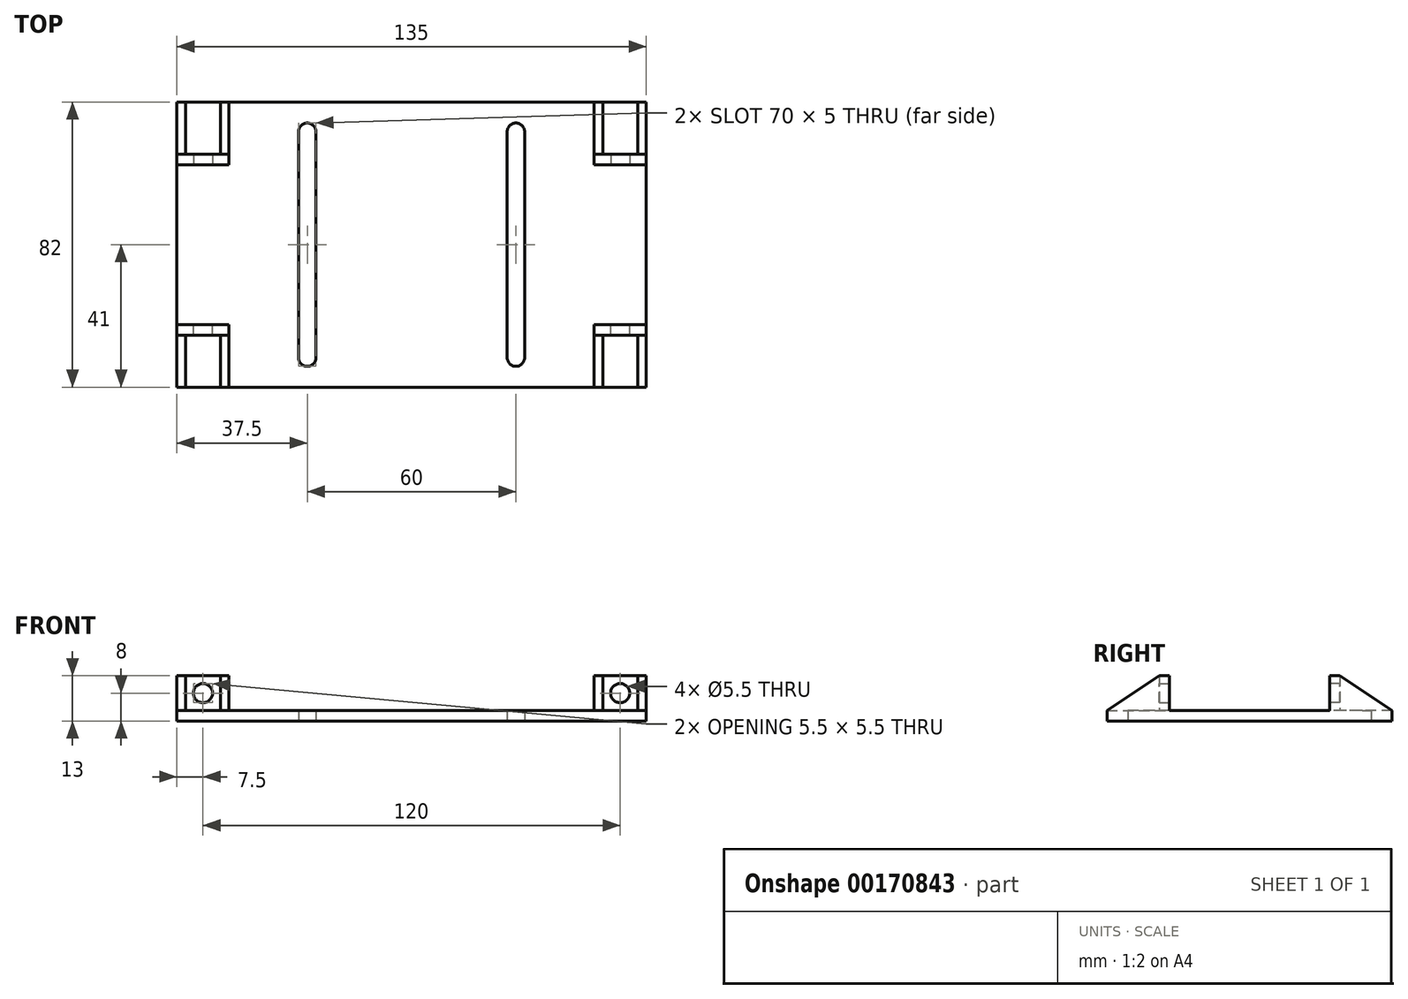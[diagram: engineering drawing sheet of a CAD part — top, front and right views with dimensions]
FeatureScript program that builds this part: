
annotation { "Feature Type Name" : "Feature", "Feature Type Description" : "" }
export const myFeature = defineFeature(function(context is Context, id is Id, definition is map)
    precondition{}
    {
        {
            var Q0;
            Q0=qCreatedBy(makeId("Top.planeOp"),FACE);
            var sketch = newSketch(context, id + "F0", { "sketchPlane" : qUnion([Q0])});
            skLineSegment(sketch, "E0", {"start": v(-67.5, -41) * mm, "end": v(67.5, -41) * mm});
            skLineSegment(sketch, "E1", {"start": v(67.5, -41) * mm, "end": v(67.5, 41) * mm});
            skLineSegment(sketch, "E2", {"start": v(67.5, 41) * mm, "end": v(-67.5, 41) * mm});
            skLineSegment(sketch, "E3", {"start": v(-67.5, 41) * mm, "end": v(-67.5, -41) * mm});
            skPoint(sketch, "E4", {"position": v(0, -41) * mm});
            skLineSegment(sketch, "E5.bottom", {"start": v(-30, 35) * mm, "end": v(-30, 35) * mm});
            skLineSegment(sketch, "E5.top", {"start": v(-30, -35) * mm, "end": v(-30, -35) * mm});
            skLineSegment(sketch, "E5.left", {"start": v(-32.5, 32.5) * mm, "end": v(-32.5, -32.5) * mm});
            skLineSegment(sketch, "E5.right", {"start": v(-27.5, 32.5) * mm, "end": v(-27.5, -32.5) * mm});
            skPoint(sketch, "E6", {"position": v(-67.5, 0) * mm});
            skLineSegment(sketch, "E7", {"start": v(-30, 71.7) * mm, "end": v(-30, -11.63) * mm, "construction": true});
            skPoint(sketch, "E7.startSnap0", {"position": v(-30, 35) * mm});
            skLineSegment(sketch, "E8", {"start": v(-39.4, 0) * mm, "end": v(-20.14, 0) * mm, "construction": true});
            skPoint(sketch, "E8.startSnap0", {"position": v(-32.5, 0) * mm});
            skPoint(sketch, "E9.visualSharp", {"position": v(-32.5, 35) * mm});
            skArc(sketch, "E9.filletArc", {"start": v(-30, 35) * mm, "mid": v(-31.77, 34.27) * mm, "end": v(-32.5, 32.5) * mm});
            skPoint(sketch, "E10.visualSharp", {"position": v(-27.5, 35) * mm});
            skArc(sketch, "E10.filletArc", {"start": v(-27.5, 32.5) * mm, "mid": v(-28.23, 34.27) * mm, "end": v(-30, 35) * mm});
            skPoint(sketch, "E11.visualSharp", {"position": v(-32.5, -35) * mm});
            skArc(sketch, "E11.filletArc", {"start": v(-32.5, -32.5) * mm, "mid": v(-31.77, -34.27) * mm, "end": v(-30, -35) * mm});
            skPoint(sketch, "E12.visualSharp", {"position": v(-27.5, -35) * mm});
            skArc(sketch, "E12.filletArc", {"start": v(-30, -35) * mm, "mid": v(-28.23, -34.27) * mm, "end": v(-27.5, -32.5) * mm});
            skLineSegment(sketch, "E13", {"start": v(0, -41) * mm, "end": v(0, 52.88) * mm, "construction": true});
            skPoint(sketch, "E13.endSnap0", {"position": v(0, 41) * mm});
            skArc(sketch, "E14.MirrorCS", {"start": v(27.5, 32.5) * mm, "mid": v(28.23, 34.27) * mm, "end": v(30, 35) * mm});
            skArc(sketch, "E15.MirrorCS", {"start": v(30, 35) * mm, "mid": v(31.77, 34.27) * mm, "end": v(32.5, 32.5) * mm});
            skLineSegment(sketch, "E16.MirrorCS", {"start": v(32.5, 32.5) * mm, "end": v(32.5, -32.5) * mm});
            skArc(sketch, "E17.MirrorCS", {"start": v(32.5, -32.5) * mm, "mid": v(31.77, -34.27) * mm, "end": v(30, -35) * mm});
            skLineSegment(sketch, "E18.MirrorCS", {"start": v(27.5, 32.5) * mm, "end": v(27.5, -32.5) * mm});
            skArc(sketch, "E19.MirrorCS", {"start": v(30, -35) * mm, "mid": v(28.23, -34.27) * mm, "end": v(27.5, -32.5) * mm});
            skSolve(sketch);
        }
        {
            var Q0;
            Q0=qSketchRegion(id+"F0",true);
            var Q1;
            Q1=makeQuery(id+"F0.imprint","IMPRINT",FACE,{"disambiguationData":[TD([[makeQuery(id+"F0.imprint","IMPRINT",EDGE,{"derivedFrom":sQuery(id+"F0.wireOp",EDGE,"T7wDZl8h-PH1E-OXKs-Syz4-WPVjGr0DlJHF")}),1.0]])]});
            extrude(context, id + "F1", {"entities" : qUnion([Q0, Q1]), "depth" : 3 * mm});
        }
        {
            var Q0;
            Q0=makeQuery(id+"F1.opExtrude","SWEPT_FACE",FACE,{"disambiguationData":[OSD([sQuery(id+"F0.wireOp",EDGE,"E1")])]});
            var sketch = newSketch(context, id + "F2", { "sketchPlane" : qUnion([Q0])});
            skLineSegment(sketch, "E20.bottom", {"start": v(-23, 3) * mm, "end": v(-26, 3) * mm});
            skLineSegment(sketch, "E20.top", {"start": v(-23, 13) * mm, "end": v(-26, 13) * mm});
            skLineSegment(sketch, "E20.left", {"start": v(-23, 3) * mm, "end": v(-23, 13) * mm});
            skLineSegment(sketch, "E20.right", {"start": v(-26, 3) * mm, "end": v(-26, 13) * mm});
            skLineSegment(sketch, "E21", {"start": v(-26, 13) * mm, "end": v(-41, 3) * mm});
            skLineSegment(sketch, "E22", {"start": v(-41, 3) * mm, "end": v(-26, 3) * mm});
            skSolve(sketch);
        }
        {
            var Q0;
            Q0=makeQuery(id+"F2.imprint","IMPRINT",FACE,{"disambiguationData":[TD([[makeQuery(id+"F2.imprint","IMPRINT",EDGE,{"derivedFrom":sQuery(id+"F2.wireOp",EDGE,"E20.bottom")}),1.0]])]});
            extrude(context, id + "F3", {"entities" : qUnion([Q0]), "operationType" : NewBodyOperationType.ADD, "oppositeDirection" : true, "depth" : 15 * mm});
        }
        {
            var Q0;
            Q0=makeQuery(id+"F2.imprint","IMPRINT",FACE,{"disambiguationData":[TD([[makeQuery(id+"F2.imprint","IMPRINT",EDGE,{"derivedFrom":sQuery(id+"F2.wireOp",EDGE,"E20.right")}),1.0]])]});
            extrude(context, id + "F4", {"entities" : qUnion([Q0]), "operationType" : NewBodyOperationType.ADD, "oppositeDirection" : true, "depth" : 15 * mm});
        }
        {
            var Q0;
            Q0=makeQuery(id+"F1.opExtrude","CAP_FACE",FACE,{"disambiguationData":[OSD([sQuery(id+"F0.wireOp",EDGE,"E0"),sQuery(id+"F0.wireOp",EDGE,"E1"),sQuery(id+"F0.wireOp",EDGE,"E2"),sQuery(id+"F0.wireOp",EDGE,"E3")])],"isStart":false});
            var sketch = newSketch(context, id + "F5", { "sketchPlane" : qUnion([Q0])});
            skLineSegment(sketch, "E23.bottom", {"start": v(65, -41) * mm, "end": v(55, -41) * mm});
            skLineSegment(sketch, "E23.top", {"start": v(65, -26) * mm, "end": v(55, -26) * mm});
            skLineSegment(sketch, "E23.left", {"start": v(65, -41) * mm, "end": v(65, -26) * mm});
            skLineSegment(sketch, "E23.right", {"start": v(55, -41) * mm, "end": v(55, -26) * mm});
            skSolve(sketch);
        }
        {
            var Q0;
            Q0=qSketchRegion(id+"F5",true);
            extrude(context, id + "F6", {"entities" : qUnion([Q0]), "operationType" : NewBodyOperationType.REMOVE, "depth" : 25 * mm});
        }
        {
            var Q0;
            Q0=makeQuery(id+"F3.opExtrude","SWEPT_FACE",FACE,{"disambiguationData":[OSD([sQuery(id+"F2.wireOp",EDGE,"E20.left")])]});
            var sketch = newSketch(context, id + "F7", { "sketchPlane" : qUnion([Q0])});
            skLineSegment(sketch, "E24", {"start": v(-52.5, 3) * mm, "end": v(-67.5, 13) * mm, "construction": true});
            skLineSegment(sketch, "E25", {"start": v(-52.5, 13) * mm, "end": v(-67.5, 3) * mm, "construction": true});
            skPoint(sketch, "E26", {"position": v(-60, 8) * mm});
            skSolve(sketch);
        }
        {
            var Q0;
            Q0=sQuery(id+"F7.wireOp",VERTEX,"E26");
            var Q1;
            Q1=makeQuery(id+"F3.opExtrude","SWEPT_BODY",BODY,{"disambiguationData":[OSD([sQuery(id+"F2.wireOp",EDGE,"E20.bottom"),sQuery(id+"F2.wireOp",EDGE,"E20.top"),sQuery(id+"F2.wireOp",EDGE,"E20.left"),sQuery(id+"F2.wireOp",EDGE,"E20.right")])]});
            var Q2;
            Q2=makeQuery(id+"F1.opExtrude","SWEPT_BODY",BODY,{"disambiguationData":[OSD([sQuery(id+"F0.wireOp",EDGE,"E0"),sQuery(id+"F0.wireOp",EDGE,"E1"),sQuery(id+"F0.wireOp",EDGE,"E2"),sQuery(id+"F0.wireOp",EDGE,"E3"),sQuery(id+"F0.wireOp",EDGE,"E5.left"),sQuery(id+"F0.wireOp",EDGE,"E5.right"),sQuery(id+"F0.wireOp",EDGE,"E9.filletArc"),sQuery(id+"F0.wireOp",EDGE,"E10.filletArc"),sQuery(id+"F0.wireOp",EDGE,"E11.filletArc"),sQuery(id+"F0.wireOp",EDGE,"E12.filletArc"),sQuery(id+"F0.wireOp",EDGE,"E14.MirrorCS"),sQuery(id+"F0.wireOp",EDGE,"E15.MirrorCS"),sQuery(id+"F0.wireOp",EDGE,"E16.MirrorCS"),sQuery(id+"F0.wireOp",EDGE,"E17.MirrorCS"),sQuery(id+"F0.wireOp",EDGE,"E18.MirrorCS"),sQuery(id+"F0.wireOp",EDGE,"E19.MirrorCS")])]});
            hole(context, id + "F8", {"style" : HoleStyle.SIMPLE, "endStyle" : HoleEndStyle.BLIND, "standardTappedOrClearance" : lookupTablePath({ "standard" : "ISO", "fit" : "Normal", "size" : "M5", "type" : "Clearance" }), "standardBlindInLast" : lookupTablePath({ "fit" : "Standard", "standard" : "ISO", "size" : "M5", "type" : "Clearance" }), "holeDiameter" : 5.5 * mm, "holeDepth" : 10 * mm, "tappedDepth" : 12 * mm, "tapClearance" : 3, "startFromSketch" : true, "locations" : qUnion([Q0]), "scope" : qUnion([Q1, Q2])});
        }
        {
            var Q0;
            Q0=makeQuery(id+"F1.opExtrude","CAP_FACE",FACE,{"disambiguationData":[OSD([sQuery(id+"F0.wireOp",EDGE,"E0"),sQuery(id+"F0.wireOp",EDGE,"E1"),sQuery(id+"F0.wireOp",EDGE,"E2"),sQuery(id+"F0.wireOp",EDGE,"E3")])],"isStart":false});
            var sketch = newSketch(context, id + "F9", { "sketchPlane" : qUnion([Q0])});
            skLineSegment(sketch, "E27", {"start": v(0, 41) * mm, "end": v(0, -15.57) * mm, "construction": true});
            skSolve(sketch);
        }
        {
            var Q0;
            Q0=makeQuery(id+"F1.opExtrude","SWEPT_BODY",BODY,{"disambiguationData":[OSD([sQuery(id+"F0.wireOp",EDGE,"E0"),sQuery(id+"F0.wireOp",EDGE,"E1"),sQuery(id+"F0.wireOp",EDGE,"E2"),sQuery(id+"F0.wireOp",EDGE,"E3")])]});
            var Q1;
            Q1=qCreatedBy(makeId("Right.planeOp"),FACE);
            mirror(context, id + "F10", {"operationType" : NewBodyOperationType.ADD, "entities" : qUnion([Q0]), "mirrorPlane" : qUnion([Q1])});
        }
        {
            var Q0;
            Q0=qCreatedBy(makeId("Right.planeOp"),FACE);
            var sketch = newSketch(context, id + "F11", { "sketchPlane" : qUnion([Q0])});
            skLineSegment(sketch, "E28", {"start": v(0, 47.04) * mm, "end": v(0, -26.32) * mm, "construction": true});
            skSolve(sketch);
        }
        {
            var Q0;
            Q0=makeQuery(id+"F1.opExtrude","SWEPT_BODY",BODY,{"disambiguationData":[OSD([sQuery(id+"F0.wireOp",EDGE,"E0"),sQuery(id+"F0.wireOp",EDGE,"E1"),sQuery(id+"F0.wireOp",EDGE,"E2"),sQuery(id+"F0.wireOp",EDGE,"E3"),sQuery(id+"F0.wireOp",EDGE,"E5.left"),sQuery(id+"F0.wireOp",EDGE,"E5.right"),sQuery(id+"F0.wireOp",EDGE,"E9.filletArc"),sQuery(id+"F0.wireOp",EDGE,"E10.filletArc"),sQuery(id+"F0.wireOp",EDGE,"E11.filletArc"),sQuery(id+"F0.wireOp",EDGE,"E12.filletArc"),sQuery(id+"F0.wireOp",EDGE,"E14.MirrorCS"),sQuery(id+"F0.wireOp",EDGE,"E15.MirrorCS"),sQuery(id+"F0.wireOp",EDGE,"E16.MirrorCS"),sQuery(id+"F0.wireOp",EDGE,"E17.MirrorCS"),sQuery(id+"F0.wireOp",EDGE,"E18.MirrorCS"),sQuery(id+"F0.wireOp",EDGE,"E19.MirrorCS")])]});
            var Q1;
            Q1=sQuery(id+"F11.wireOp",EDGE,"E28");
            circularPattern(context, id + "F12", {"operationType" : NewBodyOperationType.ADD, "entities" : qUnion([Q0]), "axis" : qUnion([Q1]), "angle" : 360 * degree, "instanceCount" : 2, "equalSpace" : true});
        }
    });
